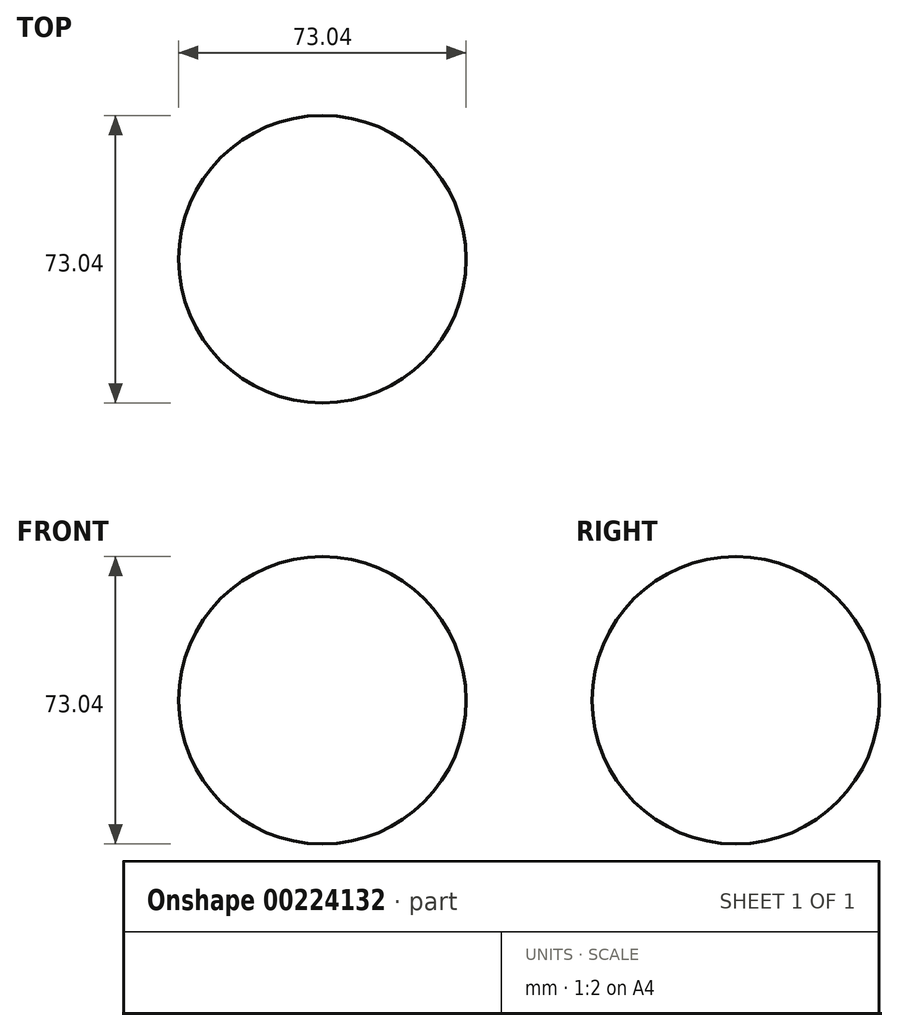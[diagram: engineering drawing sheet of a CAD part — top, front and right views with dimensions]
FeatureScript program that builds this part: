
annotation { "Feature Type Name" : "Feature", "Feature Type Description" : "" }
export const myFeature = defineFeature(function(context is Context, id is Id, definition is map)
    precondition{}
    {
        {
            var Q0;
            Q0=qCreatedBy(makeId("Front.planeOp"),FACE);
            var sketch = newSketch(context, id + "F0", { "sketchPlane" : qUnion([Q0])});
            skCircle(sketch, "E0", {"center": v(0, 0) * mm, "radius": 36.52 * mm});
            skLineSegment(sketch, "E1", {"start": v(0, 36.52) * mm, "end": v(0, -36.52) * mm});
            skSolve(sketch);
        }
        {
            var Q0;
            {var subQ0=sQuery(id+"F0.wireOp",EDGE,"E1");Q0=makeQuery(id+"F0.imprint","IMPRINT",FACE,{"disambiguationData":[TD([[makeQuery(id+"F0.imprint","IMPRINT",EDGE,{"derivedFrom":subQ0}),1.0]])]});}
            var Q1;
            Q1=sQuery(id+"F0.wireOp",EDGE,"E1");
            revolve(context, id + "F1", {"entities" : qUnion([Q0]), "axis" : qUnion([Q1]), "revolveType" : RevolveType.FULL});
        }
    });
